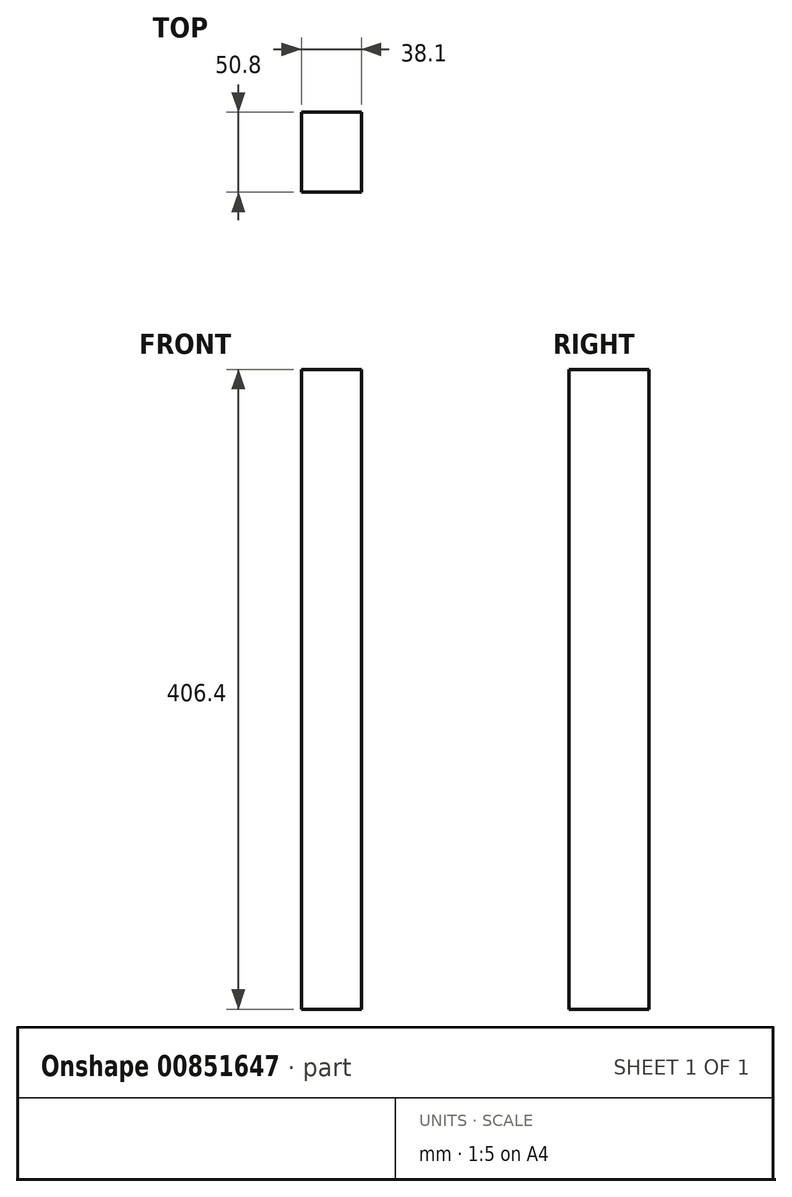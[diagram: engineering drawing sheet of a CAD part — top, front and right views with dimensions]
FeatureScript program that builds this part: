
annotation { "Feature Type Name" : "Feature", "Feature Type Description" : "" }
export const myFeature = defineFeature(function(context is Context, id is Id, definition is map)
    precondition{}
    {
        {
            var Q0;
            Q0=qCreatedBy(makeId("Front.planeOp"),FACE);
            var sketch = newSketch(context, id + "F0", { "sketchPlane" : qUnion([Q0])});
            skLineSegment(sketch, "E0", {"start": v(-24.74, 204.8) * mm, "end": v(-24.74, -201.6) * mm});
            skLineSegment(sketch, "E1", {"start": v(-24.74, 204.8) * mm, "end": v(13.36, 204.8) * mm});
            skLineSegment(sketch, "E2", {"start": v(13.36, 204.8) * mm, "end": v(13.36, -201.6) * mm});
            skLineSegment(sketch, "E3", {"start": v(13.36, -201.6) * mm, "end": v(-24.74, -201.6) * mm});
            skSolve(sketch);
        }
        {
            var Q0;
            Q0 = qSketchRegion(id + "F0", true);
            extrude(context, id + "F1", {"entities" : qUnion([Q0]), "depth" : 50.8 * mm, "offsetDistance" : 25.4 * mm});
        }
    });
